# Revit family: ANAESTIVAC 1
name_source: partatom
category: Equipement de génie climatique
revit_build: Autodesk Revit 2018 (Build: 20170223_1515(x64)
units: mm (PartAtom-declared; Revit-internal decimal feet)

## family parameters
Basée sur le plan de construction = Non
Classification = Aucun
Cote de connecteur circulaire = Utiliser le diamètre
Couper avec des vides une fois chargée = Non
Partagée = Non
Point de calcul de pièce = Non
Toujours verticalement = Oui
Type d'élément = Normal

## types (8) — shared parameters
BRANCHEMENT_TERRE = Oui
CHASSIS_ASPI_LARG = 58.3 mm
COFFRET ELEC = COFFRET ELEC STANDARD PM2 : THALASSA 341x291x168
COS_PHI = 0.9
COUPE ASPI LARG = 86.3 mm
DEPLACEMENT ASPI DROITE = 65 mm  [stored 0.213255 ft]
DEPLACEMENT ASPI GAUCHE = 507 mm
DEPLACEMENT ASPI REOULEMENT HAUTEUR = 278 mm  [stored 0.912073 ft]
DEPLACEMENT REFOULEMENT DROITE = 165 mm
DEPLACEMENT REFOULEMENT GAUCHE = 65 mm  [stored 0.213255 ft]
DOUBLE_ALIMENTATION = Non
HAUT_SILENC = 1360 mm
NBR_POLES = 3
NEUTRE = Oui
POMPES_LARG = 572 mm
POMPES_LONG = 199 mm  [stored 0.652887 ft]
TENSION_ALIM = 400 V
Zone de maintenance 1 = Oui
Zone de maintenance coffret = Oui
zero-valued in all types: HAUTEUR, LARGEUR, LONGUEUR

## per-type parameters (varying)
| type | COUPE REFOULEMENT | DEBIT_ASPI_VIDE | DEBIT_REFOUL_VIDE | DESCR_ALIM_X | DESCR_ASPI | DESCR_REFOUL | DIAM_ASPI_VIDE | DIAM_REFOUL_VIDE | ECARTEMENT_ASPI_REFOUL | HAUTEUR_ASPI | HAUT_ASPI_REFOUL | HAUT_POMPE | HAUT_VANNE | NIVEAU_SONORE(dB(A)) | OFFSET_LONG_POMPE | POIDS(Kg) | POMPES | PUISS_APPARENTE | PUISS_ELECT | TYPE_FILTRE | TYPE_SUPPORT | TYPE_VANNE | VERSION_AUTOMATIQUE |
| Y006V - AUTOMATIQUE | 98 mm  [stored 0.321522 ft] | 75.0 m³/h | 75.0 m³/h | Alimentation électrique, 5G1mm² | Aspiration Vide; 75m3/h; G1"1/4"MALE | Refoulement Vide; 75m3/h; Ø44 | 32 mm  [stored 0.104987 ft] | 44 mm  [stored 0.144357 ft] | 100 mm  [stored 0.328084 ft] | 84 mm  [stored 0.275591 ft] | 278 mm  [stored 0.912073 ft] | 240 mm  [stored 0.787402 ft] | 350 mm  [stored 1.14829 ft] | 58 | 2 mm  [stored 0.00656168 ft] | 35 mm  [stored 0.114829 ft] | PAV_ANAESTIVAC 2 : Y006V | 422 VA | 0 kW | FILTRE SILENCIEUX FS : F75 | SUPPORT ANAESTIVAC 1 : Y006V - Y011V | VANNE ER20 : DN20 - G3/4" - FF | Oui |
| Y006V - CONTROLE A DISTANCE | 98 mm  [stored 0.321522 ft] | 75.0 m³/h | 75.0 m³/h | Alimentation électrique, 5G1mm² | Aspiration Vide; 75m3/h; G1"1/4"MALE | Refoulement Vide; 75m3/h; Ø44 | 32 mm  [stored 0.104987 ft] | 44 mm  [stored 0.144357 ft] | 100 mm  [stored 0.328084 ft] | 84 mm  [stored 0.275591 ft] | 278 mm  [stored 0.912073 ft] | 240 mm  [stored 0.787402 ft] | 330 mm | 58 | 2 mm  [stored 0.00656168 ft] | 35 mm  [stored 0.114829 ft] | PAV_ANAESTIVAC 2 : Y006V | 422 VA | 0 kW | FILTRE SILENCIEUX FS : F75 | SUPPORT ANAESTIVAC 1 : Y006V - Y011V | VANNE ER20 : DN20 - G3/4" - FF | Non |
| Y011V - AUTOMATIQUE | 60 mm  [stored 0.19685 ft] | 144.0 m³/h | 144.0 m³/h | Alimentation électrique, 5G1.5mm² | Aspiration Vide; 144m3/h; G1"1/2"MALE | Refoulement Vide; 144m3/h; Ø44 | 40 mm  [stored 0.131234 ft] | 44 mm  [stored 0.144357 ft] | 115 mm  [stored 0.377297 ft] | 81 mm  [stored 0.265748 ft] | 286 mm | 240 mm  [stored 0.787402 ft] | 360 mm  [stored 1.1811 ft] | 64 | 2 mm  [stored 0.00656168 ft] | 45 mm  [stored 0.147638 ft] | PAV_ANAESTIVAC 2 : Y011V | 1000 VA | 1 kW | FILTRE SILENCIEUX FS : F75 | SUPPORT ANAESTIVAC 1 : Y006V - Y011V | VANNE ER20 : DN25 - G1" - FF | Oui |
| Y011V - CONTROLE A DISTANCE | 60 mm  [stored 0.19685 ft] | 144.0 m³/h | 144.0 m³/h | Alimentation électrique, 5G1.5mm² | Aspiration Vide; 144m3/h; G1"1/2"MALE | Refoulement Vide; 144m3/h; Ø44 | 40 mm  [stored 0.131234 ft] | 44 mm  [stored 0.144357 ft] | 115 mm  [stored 0.377297 ft] | 81 mm  [stored 0.265748 ft] | 286 mm | 240 mm  [stored 0.787402 ft] | 340 mm  [stored 1.11549 ft] | 64 | 2 mm  [stored 0.00656168 ft] | 45 mm  [stored 0.147638 ft] | PAV_ANAESTIVAC 2 : Y011V | 1000 VA | 1 kW | FILTRE SILENCIEUX FS : F75 | SUPPORT ANAESTIVAC 1 : Y006V - Y011V | VANNE ER20 : DN25 - G1" - FF | Non |
| Y020V - AUTOMATIQUE | 69 mm  [stored 0.226378 ft] | 210.0 m³/h | 210.0 m³/h | Alimentation électrique, 5G1.5mm² | Aspiration Vide; 210m3/h; G2"MALE | Refoulement Vide; 210m3/h; Ø60 | 50 mm  [stored 0.164042 ft] | 60 mm  [stored 0.19685 ft] | 120 mm  [stored 0.393701 ft] | 67 mm  [stored 0.219816 ft] | 328 mm  [stored 1.07612 ft] | 280 mm  [stored 0.918635 ft] | 400 mm  [stored 1.31234 ft] | 68 | 2 mm  [stored 0.00656168 ft] | 55 mm  [stored 0.180446 ft] | PAV_ANAESTIVAC 2 : Y020V | 1667 VA | 2 kW | FILTRE SILENCIEUX FS : F125 | SUPPORT ANAESTIVAC 1 : Y020V - Y030V | VANNE ER20 : DN32 - G1"1/4 - FF | Oui |
| Y020V - CONTROLE A DISTANCE | 69 mm  [stored 0.226378 ft] | 210.0 m³/h | 210.0 m³/h | Alimentation électrique, 5G1.5mm² | Aspiration Vide; 210m3/h; G2"MALE | Refoulement Vide; 210m3/h; Ø60 | 50 mm  [stored 0.164042 ft] | 60 mm  [stored 0.19685 ft] | 120 mm  [stored 0.393701 ft] | 67 mm  [stored 0.219816 ft] | 328 mm  [stored 1.07612 ft] | 280 mm  [stored 0.918635 ft] | 380 mm | 68 | 2 mm  [stored 0.00656168 ft] | 55 mm  [stored 0.180446 ft] | PAV_ANAESTIVAC 2 : Y020V | 1667 VA | 2 kW | FILTRE SILENCIEUX FS : F125 | SUPPORT ANAESTIVAC 1 : Y020V - Y030V | VANNE ER20 : DN32 - G1"1/4 - FF | Non |
| Y030V - AUTOMATIQUE | 142 mm  [stored 0.465879 ft] | 306.0 m³/h | 306.0 m³/h | Alimentation électrique, 5G2.5mm² | Aspiration Vide; 306m3/h; G2"MALE | Refoulement Vide; 306m3/h; Ø60 | 50 mm  [stored 0.164042 ft] | 60 mm  [stored 0.19685 ft] | 125 mm  [stored 0.410105 ft] | 58 mm  [stored 0.190289 ft] | 333 mm  [stored 1.09252 ft] | 280 mm  [stored 0.918635 ft] | 450 mm | 70 | 30 mm  [stored 0.0984252 ft] | 70 mm  [stored 0.229659 ft] | PAV_ANAESTIVAC 2 : Y030V | 2444 VA | 2 kW | FILTRE SILENCIEUX FS : F125 | SUPPORT ANAESTIVAC 1 : Y020V - Y030V | VANNE ER20 : DN32 - G1"1/4 - FF | Oui |
| Y030V - CONTROLE A DISTANCE | 142 mm  [stored 0.465879 ft] | 306.0 m³/h | 306.0 m³/h | Alimentation électrique, 5G2.5mm² | Aspiration Vide; 306m3/h; G2"MALE | Refoulement Vide; 306m3/h; Ø60 | 50 mm  [stored 0.164042 ft] | 60 mm  [stored 0.19685 ft] | 125 mm  [stored 0.410105 ft] | 58 mm  [stored 0.190289 ft] | 333 mm  [stored 1.09252 ft] | 280 mm  [stored 0.918635 ft] | 450 mm | 70 | 30 mm  [stored 0.0984252 ft] | 70 mm  [stored 0.229659 ft] | PAV_ANAESTIVAC 2 : Y030V | 2444 VA | 2 kW | FILTRE SILENCIEUX FS : F125 | SUPPORT ANAESTIVAC 1 : Y020V - Y030V | VANNE ER20 : DN32 - G1"1/4 - FF | Non |

note: [stored X ft] marks values corroborated as IEEE doubles in the binary element streams (Revit-internal decimal feet)

## geometry (parser evidence)
native form markers: Sweep x8
no freeform markers — native parametric forms only
